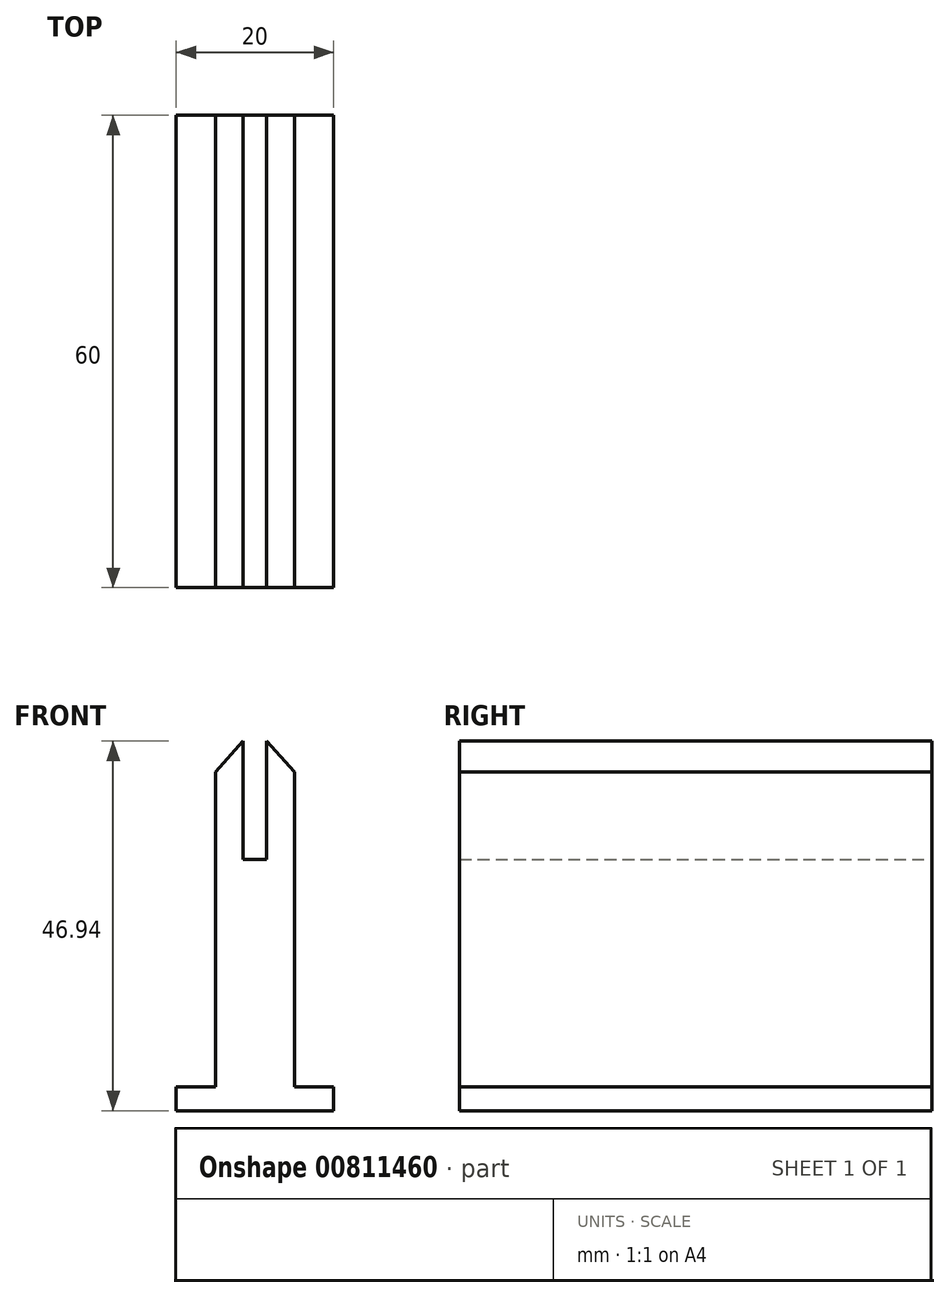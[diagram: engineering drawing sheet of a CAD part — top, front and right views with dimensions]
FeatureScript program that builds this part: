
annotation { "Feature Type Name" : "Feature", "Feature Type Description" : "" }
export const myFeature = defineFeature(function(context is Context, id is Id, definition is map)
    precondition{}
    {
        {
            var Q0;
            Q0=qCreatedBy(makeId("Front.planeOp"),FACE);
            var sketch = newSketch(context, id + "F0", { "sketchPlane" : qUnion([Q0])});
            skLineSegment(sketch, "E0", {"start": v(0, 0) * mm, "end": v(10, 0) * mm});
            skLineSegment(sketch, "E1", {"start": v(10, 0) * mm, "end": v(10, 3) * mm});
            skLineSegment(sketch, "E2", {"start": v(10, 3) * mm, "end": v(5, 3) * mm});
            skLineSegment(sketch, "E3", {"start": v(5, 3) * mm, "end": v(5, 43) * mm});
            skLineSegment(sketch, "E4", {"start": v(5, 43) * mm, "end": v(1.5, 46.94) * mm});
            skLineSegment(sketch, "E5", {"start": v(1.5, 46.94) * mm, "end": v(1.5, 31.94) * mm});
            skLineSegment(sketch, "E6", {"start": v(1.5, 31.94) * mm, "end": v(0, 31.94) * mm});
            skLineSegment(sketch, "E7", {"start": v(0, 31.94) * mm, "end": v(0, 0) * mm});
            skLineSegment(sketch, "E8.MirrorCS", {"start": v(-5, 3) * mm, "end": v(-5, 43) * mm});
            skLineSegment(sketch, "E9.MirrorCS", {"start": v(-5, 43) * mm, "end": v(-1.5, 46.94) * mm});
            skLineSegment(sketch, "E10.MirrorCS", {"start": v(-1.5, 46.94) * mm, "end": v(-1.5, 31.94) * mm});
            skLineSegment(sketch, "E11.MirrorCS", {"start": v(-10, 3) * mm, "end": v(-5, 3) * mm});
            skLineSegment(sketch, "E12.MirrorCS", {"start": v(-10, 0) * mm, "end": v(-10, 3) * mm});
            skLineSegment(sketch, "E13.MirrorCS", {"start": v(0, 0) * mm, "end": v(-10, 0) * mm});
            skLineSegment(sketch, "E14.MirrorCS", {"start": v(-1.5, 31.94) * mm, "end": v(0, 31.94) * mm});
            skSolve(sketch);
        }
        {
            var Q0;
            Q0 = qSketchRegion(id + "F0", true);
            extrude(context, id + "F1", {"entities" : qUnion([Q0]), "depth" : 60 * mm, "offsetDistance" : 25 * mm});
        }
    });
